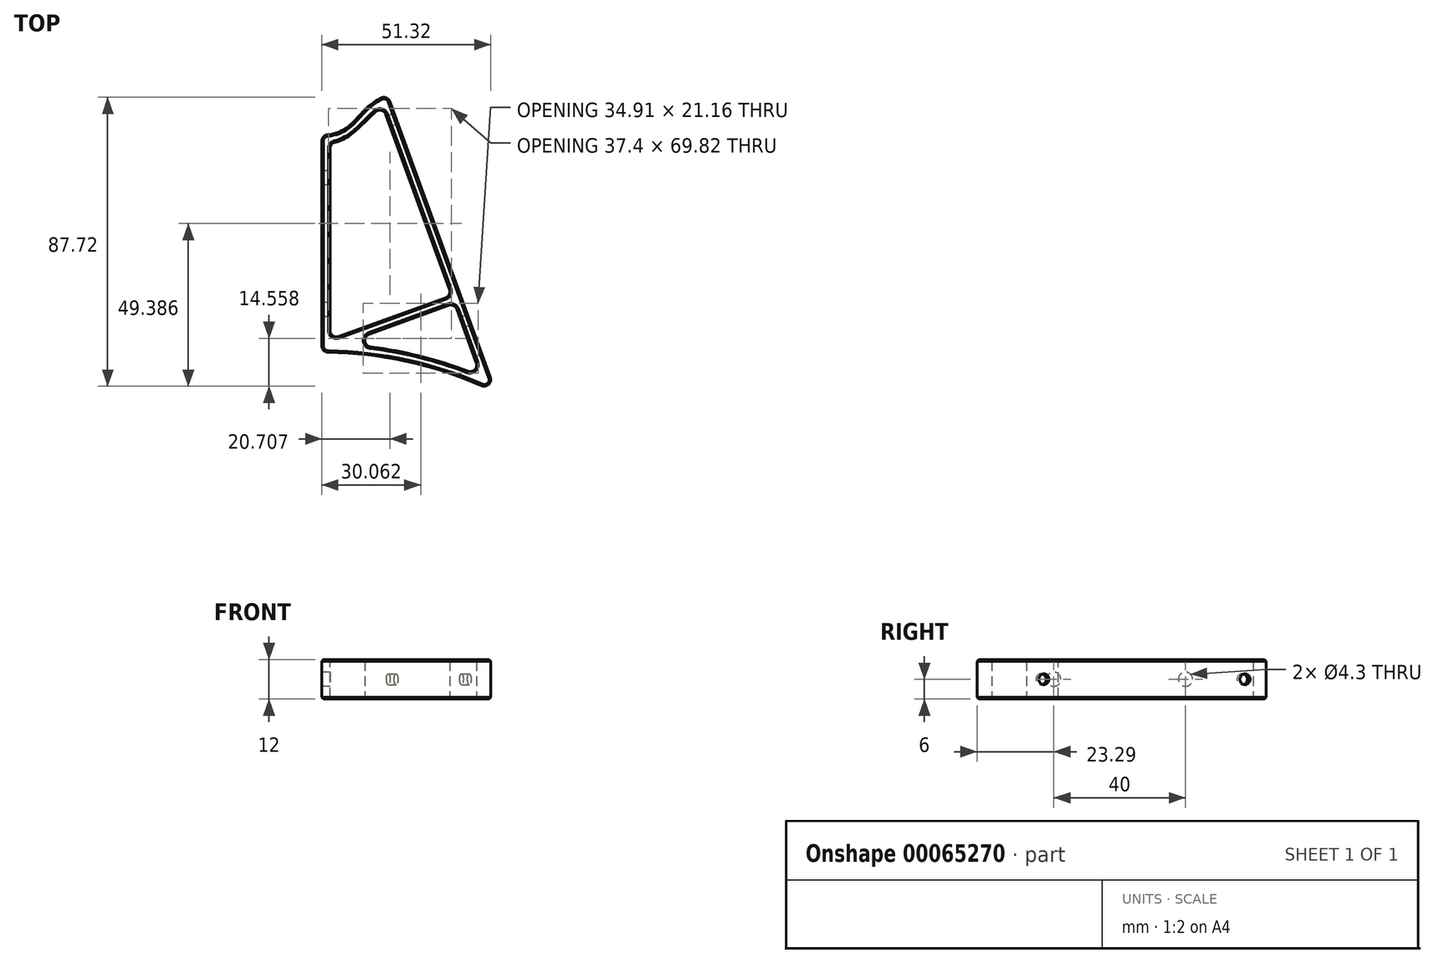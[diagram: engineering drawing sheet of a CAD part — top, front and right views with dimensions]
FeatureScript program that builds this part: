
annotation { "Feature Type Name" : "Feature", "Feature Type Description" : "" }
export const myFeature = defineFeature(function(context is Context, id is Id, definition is map)
    precondition{}
    {
        {
            var Q0;
            Q0=qCreatedBy(makeId("Top.planeOp"),FACE);
            var sketch = newSketch(context, id + "F0", { "sketchPlane" : qUnion([Q0])});
            skLineSegment(sketch, "E0", {"start": v(0, 0) * mm, "end": v(0, 66) * mm});
            skLineSegment(sketch, "E1", {"start": v(20, 78.1) * mm, "end": v(52.83, -12.1) * mm});
            skArc(sketch, "E2", {"start": v(52.83, -12.1) * mm, "mid": v(27.1, -3.07) * mm, "end": v(0, 0) * mm});
            skLineSegment(sketch, "E3", {"start": v(0, 66) * mm, "end": v(0, 78.1) * mm, "construction": true});
            skLineSegment(sketch, "E4", {"start": v(0, 78.1) * mm, "end": v(20, 78.1) * mm, "construction": true});
            skLineSegment(sketch, "E5", {"start": v(0, 0) * mm, "end": v(0, -12.1) * mm, "construction": true});
            skLineSegment(sketch, "E6", {"start": v(0, -12.1) * mm, "end": v(52.83, -12.1) * mm, "construction": true});
            skLineSegment(sketch, "E7.0", {"start": v(2.5, 3.82) * mm, "end": v(2.5, 63.64) * mm});
            skArc(sketch, "E7.1", {"start": v(48.44, -7.36) * mm, "mid": v(27.58, -0.6) * mm, "end": v(5.86, 2.37) * mm});
            skLineSegment(sketch, "E7.2", {"start": v(18.57, 74.71) * mm, "end": v(39.47, 17.27) * mm});
            skLineSegment(sketch, "E8", {"start": v(2.5, 3.82) * mm, "end": v(39.47, 17.27) * mm});
            skLineSegment(sketch, "E9", {"start": v(5.86, 2.37) * mm, "end": v(40.33, 14.91) * mm});
            skLineSegment(sketch, "E10", {"start": v(2.5, 2.48) * mm, "end": v(39.9, 16.1) * mm, "construction": true});
            skLineSegment(sketch, "E11.trimOffspring", {"start": v(40.33, 14.91) * mm, "end": v(48.44, -7.36) * mm});
            skFitSpline(sketch, "E12", {"points": [v(0, 66) * mm, v(20, 78.1) * mm], "startDerivative": vector(32.6, 0) * mm, "endDerivative": vector(30, 10.92) * mm});
            skLineSegment(sketch, "E13", {"start": v(0, 66) * mm, "end": v(21.74, 66) * mm, "construction": true});
            skLineSegment(sketch, "E14", {"start": v(20, 78.1) * mm, "end": v(0, 70.83) * mm, "construction": true});
            skFitSpline(sketch, "E15", {"points": [v(2.5, 63.64) * mm, v(18.57, 74.71) * mm], "startDerivative": vector(19.89, 0) * mm, "endDerivative": vector(12.58, 6.93) * mm});
            skLineSegment(sketch, "E16", {"start": v(2.5, 63.64) * mm, "end": v(22.6, 63.64) * mm, "construction": true});
            skLineSegment(sketch, "E17", {"start": v(18.57, 74.71) * mm, "end": v(17.36, 76.91) * mm});
            skLineSegment(sketch, "E18", {"start": v(17.36, 76.91) * mm, "end": v(9.03, 72.32) * mm, "construction": true});
            skLineSegment(sketch, "E19", {"start": v(18.57, 74.71) * mm, "end": v(7.4, 68.56) * mm, "construction": true});
            skSolve(sketch);
        }
        {
            var Q0;
            Q0=makeQuery(id+"F0.imprint","IMPRINT",FACE,{"disambiguationData":[TD([[makeQuery(id+"F0.imprint","IMPRINT",EDGE,{"derivedFrom":sQuery(id+"F0.wireOp",EDGE,"E0")}),-1.0]])]});
            extrude(context, id + "F1", {"entities" : qUnion([Q0]), "endBound" : BoundingType.SYMMETRIC, "depth" : 12 * mm});
        }
        {
            var Q0;
            Q0=makeQuery(id+"F1.opExtrude","SWEPT_FACE",FACE,{"disambiguationData":[OSD([sQuery(id+"F0.wireOp",EDGE,"E0")])]});
            var sketch = newSketch(context, id + "F2", { "sketchPlane" : qUnion([Q0])});
            skCircle(sketch, "E20", {"center": v(-53, 0) * mm, "radius": 2.15 * mm});
            skCircle(sketch, "E21", {"center": v(-13, 0) * mm, "radius": 2.15 * mm});
            skSolve(sketch);
        }
        {
            var Q0;
            Q0=makeQuery(id+"F2.imprint","IMPRINT",FACE,{"disambiguationData":[TD([[makeQuery(id+"F2.imprint","IMPRINT",EDGE,{"derivedFrom":sQuery(id+"F2.wireOp",EDGE,"E21")}),1.0]])]});
            var Q1;
            Q1=makeQuery(id+"F2.imprint","IMPRINT",FACE,{"disambiguationData":[TD([[makeQuery(id+"F2.imprint","IMPRINT",EDGE,{"derivedFrom":sQuery(id+"F2.wireOp",EDGE,"E20")}),1.0]])]});
            var Q2;
            Q2=makeQuery(id+"F1.opExtrude","SWEPT_FACE",FACE,{"disambiguationData":[OSD([sQuery(id+"F0.wireOp",EDGE,"E7.0")])]});
            extrude(context, id + "F3", {"entities" : qUnion([Q0, Q1]), "operationType" : NewBodyOperationType.REMOVE, "endBound" : BoundingType.UP_TO_SURFACE, "oppositeDirection" : true, "endBoundEntityFace" : qUnion([Q2]), "depth" : 25 * mm});
        }
        {
            var Q0;
            Q0=makeQuery(id+"F1.opExtrude","SWEPT_FACE",FACE,{"disambiguationData":[OSD([sQuery(id+"F0.wireOp",EDGE,"E1")])]});
            var sketch = newSketch(context, id + "F4", { "sketchPlane" : qUnion([Q0])});
            skCircle(sketch, "E22", {"center": v(59.05, 0) * mm, "radius": 1.65 * mm});
            skCircle(sketch, "E23", {"center": v(-5.95, 0) * mm, "radius": 1.65 * mm});
            skSolve(sketch);
        }
        {
            var Q0;
            Q0=makeQuery(id+"F4.imprint","IMPRINT",FACE,{"disambiguationData":[TD([[makeQuery(id+"F4.imprint","IMPRINT",EDGE,{"derivedFrom":sQuery(id+"F4.wireOp",EDGE,"E22")}),1.0]])]});
            var Q1;
            Q1=makeQuery(id+"F4.imprint","IMPRINT",FACE,{"disambiguationData":[TD([[makeQuery(id+"F4.imprint","IMPRINT",EDGE,{"derivedFrom":sQuery(id+"F4.wireOp",EDGE,"E23")}),1.0]])]});
            var Q2;
            Q2=makeQuery(id+"F1.opExtrude","SWEPT_FACE",FACE,{"disambiguationData":[OSD([sQuery(id+"F0.wireOp",EDGE,"E7.2")])]});
            extrude(context, id + "F5", {"entities" : qUnion([Q0, Q1]), "operationType" : NewBodyOperationType.REMOVE, "endBound" : BoundingType.UP_TO_SURFACE, "oppositeDirection" : true, "endBoundEntityFace" : qUnion([Q2]), "depth" : 25 * mm});
        }
        {
            var Q0;
            Q0=makeQuery(id+"F1.opExtrude","SWEPT_EDGE",EDGE,{"disambiguationData":[OSD([sQuery(id+"F0.wireOp",EDGE,"E7.0"),sQuery(id+"F0.wireOp",EDGE,"E15")])]});
            var Q1;
            Q1=makeQuery(id+"F1.opExtrude","SWEPT_EDGE",EDGE,{"disambiguationData":[OSD([sQuery(id+"F0.wireOp",EDGE,"E7.2"),sQuery(id+"F0.wireOp",EDGE,"E15")])]});
            var Q2;
            Q2=makeQuery(id+"F1.opExtrude","SWEPT_EDGE",EDGE,{"disambiguationData":[OSD([sQuery(id+"F0.wireOp",EDGE,"E9"),sQuery(id+"F0.wireOp",EDGE,"E11.trimOffspring")])]});
            var Q3;
            Q3=makeQuery(id+"F1.opExtrude","SWEPT_EDGE",EDGE,{"disambiguationData":[OSD([sQuery(id+"F0.wireOp",EDGE,"E7.2"),sQuery(id+"F0.wireOp",EDGE,"E8")])]});
            var Q4;
            Q4=makeQuery(id+"F1.opExtrude","SWEPT_EDGE",EDGE,{"disambiguationData":[OSD([sQuery(id+"F0.wireOp",EDGE,"E1"),sQuery(id+"F0.wireOp",EDGE,"E12")])]});
            var Q5;
            Q5=makeQuery(id+"F1.opExtrude","SWEPT_EDGE",EDGE,{"disambiguationData":[OSD([sQuery(id+"F0.wireOp",EDGE,"E0"),sQuery(id+"F0.wireOp",EDGE,"E12")])]});
            var Q6;
            Q6=makeQuery(id+"F1.opExtrude","SWEPT_EDGE",EDGE,{"disambiguationData":[OSD([sQuery(id+"F0.wireOp",EDGE,"E1"),sQuery(id+"F0.wireOp",EDGE,"E2")])]});
            var Q7;
            Q7=makeQuery(id+"F1.opExtrude","SWEPT_EDGE",EDGE,{"disambiguationData":[OSD([sQuery(id+"F0.wireOp",EDGE,"E7.1"),sQuery(id+"F0.wireOp",EDGE,"E11.trimOffspring")])]});
            var Q8;
            Q8=makeQuery(id+"F1.opExtrude","SWEPT_EDGE",EDGE,{"disambiguationData":[OSD([sQuery(id+"F0.wireOp",EDGE,"E7.1"),sQuery(id+"F0.wireOp",EDGE,"E9")])]});
            var Q9;
            Q9=makeQuery(id+"F1.opExtrude","SWEPT_EDGE",EDGE,{"disambiguationData":[OSD([sQuery(id+"F0.wireOp",EDGE,"E7.0"),sQuery(id+"F0.wireOp",EDGE,"E8")])]});
            var Q10;
            Q10=makeQuery(id+"F1.opExtrude","SWEPT_EDGE",EDGE,{"disambiguationData":[OSD([sQuery(id+"F0.wireOp",EDGE,"E0"),sQuery(id+"F0.wireOp",EDGE,"E2")])]});
            fillet(context, id + "F6", {"entities" : qUnion([Q0, Q1, Q2, Q3, Q4, Q5, Q6, Q7, Q8, Q9, Q10]), "radius" : 2 * mm, "tangentPropagation" : true, "allowEdgeOverflow" : false});
        }
        {
            var Q0;
            Q0=makeQuery(id+"F1.opExtrude","CAP_EDGE",EDGE,{"disambiguationData":[OSD([sQuery(id+"F0.wireOp",EDGE,"E0")])],"isStart":false});
            var Q1;
            Q1=makeQuery(id+"F1.opExtrude","CAP_EDGE",EDGE,{"disambiguationData":[OSD([sQuery(id+"F0.wireOp",EDGE,"E8")])],"isStart":false});
            var Q2;
            Q2=makeQuery(id+"F1.opExtrude","CAP_EDGE",EDGE,{"disambiguationData":[OSD([sQuery(id+"F0.wireOp",EDGE,"E9")])],"isStart":false});
            var Q3;
            Q3=makeQuery(id+"F1.opExtrude","CAP_EDGE",EDGE,{"disambiguationData":[OSD([sQuery(id+"F0.wireOp",EDGE,"E0")])],"isStart":true});
            var Q4;
            Q4=makeQuery(id+"F1.opExtrude","CAP_EDGE",EDGE,{"disambiguationData":[OSD([sQuery(id+"F0.wireOp",EDGE,"E7.0")])],"isStart":true});
            var Q5;
            Q5=makeQuery(id+"F1.opExtrude","CAP_EDGE",EDGE,{"disambiguationData":[OSD([sQuery(id+"F0.wireOp",EDGE,"E9")])],"isStart":true});
            chamfer(context, id + "F7", {"entities" : qUnion([Q0, Q1, Q2, Q3, Q4, Q5]), "width" : 0.5 * mm, "tangentPropagation" : true});
        }
    });
